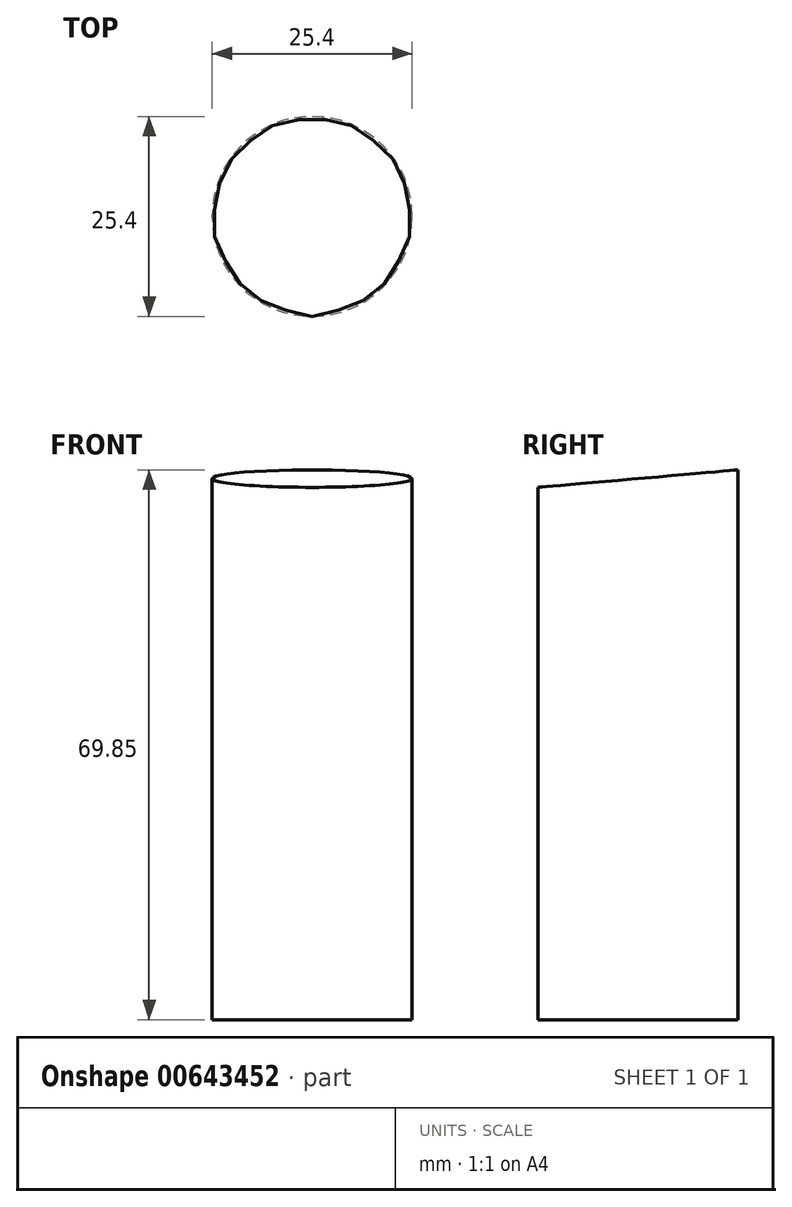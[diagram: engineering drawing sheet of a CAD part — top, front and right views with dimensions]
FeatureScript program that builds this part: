
annotation { "Feature Type Name" : "Feature", "Feature Type Description" : "" }
export const myFeature = defineFeature(function(context is Context, id is Id, definition is map)
    precondition{}
    {
        {
            var Q0;
            Q0=qCreatedBy(makeId("Top.planeOp"),FACE);
            var sketch = newSketch(context, id + "F0", { "sketchPlane" : qUnion([Q0])});
            skCircle(sketch, "E0", {"center": v(0, 0) * mm, "radius": 12.7 * mm});
            skSolve(sketch);
        }
        {
            var Q0;
            Q0=makeQuery(id+"F0.imprint","IMPRINT",FACE,{"disambiguationData":[TD([[makeQuery(id+"F0.imprint","IMPRINT",EDGE,{"derivedFrom":sQuery(id+"F0.wireOp",EDGE,"E0")}),1.0]])]});
            extrude(context, id + "F1", {"entities" : qUnion([Q0]), "depth" : 69.85 * mm, "offsetDistance" : 25.4 * mm});
        }
        {
            var Q0;
            Q0=qCreatedBy(makeId("Right.planeOp"),FACE);
            var sketch = newSketch(context, id + "F2", { "sketchPlane" : qUnion([Q0])});
            skLineSegment(sketch, "E1.0", {"start": v(-12.7, 69.85) * mm, "end": v(12.7, 69.85) * mm});
            skLineSegment(sketch, "E2", {"start": v(12.7, 69.85) * mm, "end": v(-12.7, 67.63) * mm});
            skLineSegment(sketch, "E3", {"start": v(-12.7, 69.85) * mm, "end": v(-12.7, 67.63) * mm});
            skSolve(sketch);
        }
        {
            var Q0;
            Q0=qSketchRegion(id+"F2",true);
            extrude(context, id + "F3", {"entities" : qUnion([Q0]), "operationType" : NewBodyOperationType.REMOVE, "depth" : 50.8 * mm, "offsetDistance" : 25.4 * mm, "symmetric" : true});
        }
    });
